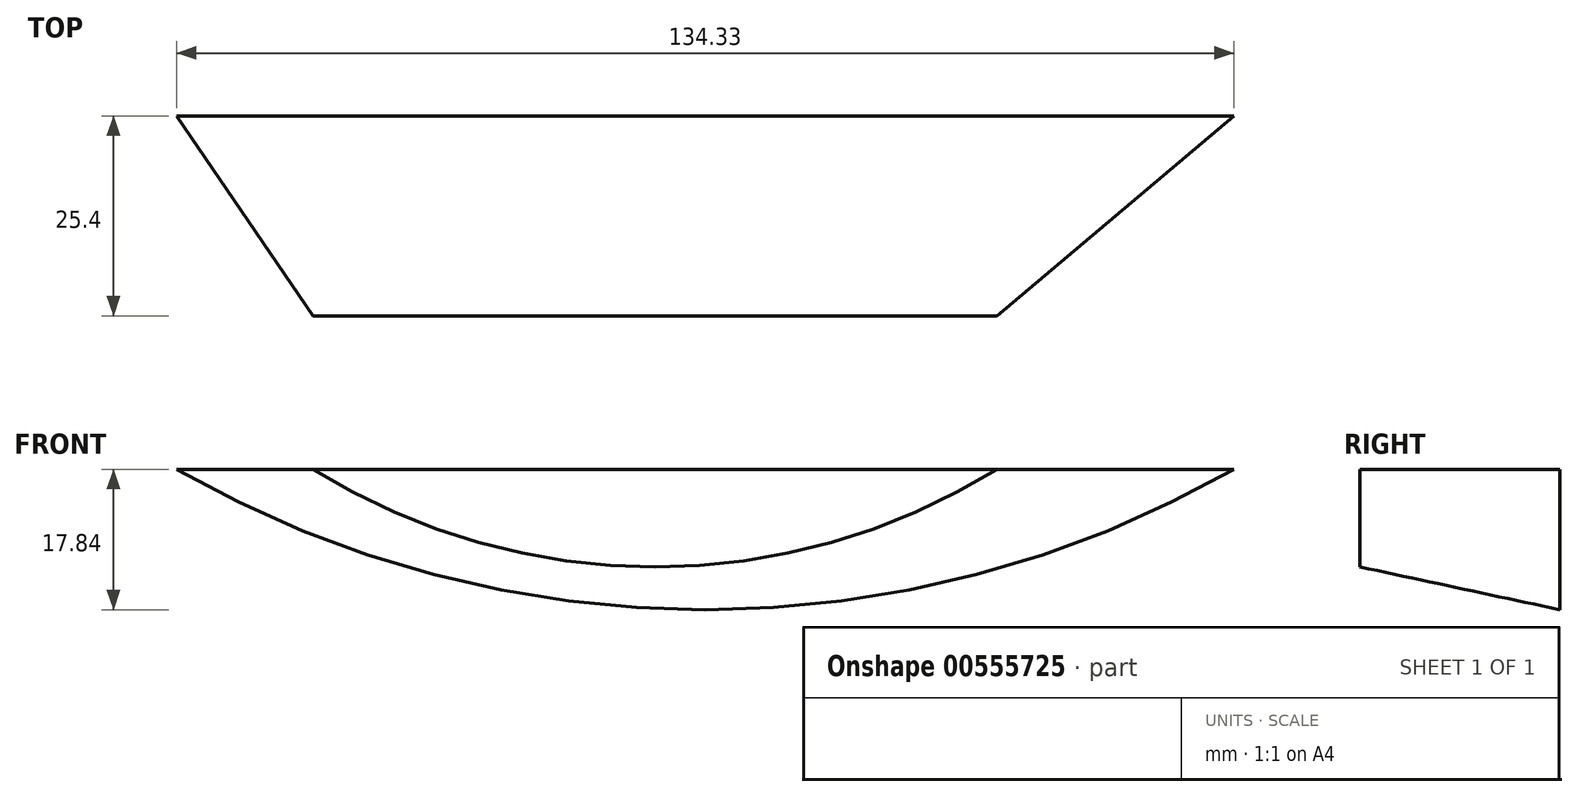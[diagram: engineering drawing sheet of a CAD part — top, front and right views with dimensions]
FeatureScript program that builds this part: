
annotation { "Feature Type Name" : "Feature", "Feature Type Description" : "" }
export const myFeature = defineFeature(function(context is Context, id is Id, definition is map)
    precondition{}
    {
        {
            var Q0;
            Q0=qCreatedBy(makeId("Top.planeOp"),FACE);
            var sketch = newSketch(context, id + "F0", { "sketchPlane" : qUnion([Q0])});
            skLineSegment(sketch, "E0", {"start": v(-69.36, 0) * mm, "end": v(64.97, 0) * mm});
            skLineSegment(sketch, "E1", {"start": v(64.97, 0) * mm, "end": v(64.97, -7.73) * mm});
            skLineSegment(sketch, "E2", {"start": v(-69.36, 0) * mm, "end": v(-69.36, -7.73) * mm});
            skArc(sketch, "E3", {"start": v(-69.36, -7.73) * mm, "mid": v(-2.2, -21.41) * mm, "end": v(64.97, -7.73) * mm});
            skLineSegment(sketch, "E4", {"start": v(64.97, -7.73) * mm, "end": v(-69.36, -7.73) * mm});
            skSolve(sketch);
        }
        {
            var Q0;
            Q0=qCreatedBy(makeId("Front.planeOp"),FACE);
            var sketch = newSketch(context, id + "F1", { "sketchPlane" : qUnion([Q0])});
            skLineSegment(sketch, "E5.0", {"start": v(-69.36, 0) * mm, "end": v(64.97, 0) * mm});
            skArc(sketch, "E6", {"start": v(-69.36, 0) * mm, "mid": v(-2.2, -17.84) * mm, "end": v(64.97, 0) * mm});
            skSolve(sketch);
        }
        {
            var Q0;
            Q0=qCreatedBy(makeId("Front.planeOp"),FACE);
            cPlane(context, id + "F2", {"entities" : qUnion([Q0]), "cplaneType" : CPlaneType.OFFSET, "offset" : 25.4 * mm, "width" : 152.4 * mm, "height" : 152.4 * mm});
        }
        {
            var Q0;
            Q0=qCreatedBy(id+"F2.planeOp",FACE);
            var sketch = newSketch(context, id + "F3", { "sketchPlane" : qUnion([Q0])});
            skLineSegment(sketch, "E7", {"start": v(34.89, 0) * mm, "end": v(-52.02, 0) * mm});
            skArc(sketch, "E8", {"start": v(-52.02, 0) * mm, "mid": v(-8.57, -12.4) * mm, "end": v(34.89, 0) * mm});
            skSolve(sketch);
        }
        {
            var Q0;
            Q0=makeQuery(id+"F1.imprint","IMPRINT",FACE,{"disambiguationData":[TD([[makeQuery(id+"F1.imprint","IMPRINT",EDGE,{"derivedFrom":sQuery(id+"F1.wireOp",EDGE,"E5.0")}),-1.0]])]});
            var Q1;
            Q1=makeQuery(id+"F3.imprint","IMPRINT",FACE,{"disambiguationData":[TD([[makeQuery(id+"F3.imprint","IMPRINT",EDGE,{"derivedFrom":sQuery(id+"F3.wireOp",EDGE,"E7")}),1.0]])]});
            var Q2;
            Q2=makeQuery(id+"F1.imprint","IMPRINT",FACE,{"disambiguationData":[TD([[makeQuery(id+"F1.imprint","IMPRINT",EDGE,{"derivedFrom":sQuery(id+"F1.wireOp",EDGE,"E5.0")}),-1.0]])]});
            var Q3;
            Q3=makeQuery(id+"F3.imprint","IMPRINT",FACE,{"disambiguationData":[TD([[makeQuery(id+"F3.imprint","IMPRINT",EDGE,{"derivedFrom":sQuery(id+"F3.wireOp",EDGE,"E7")}),1.0]])]});
            loft(context, id + "F4", {"bodyType" : ToolBodyType.SURFACE, "sheetProfilesArray" : [{ "sheetProfileEntities" : qUnion([Q0]) }, { "sheetProfileEntities" : qUnion([Q1]) }], "wireProfilesArray" : [{ "wireProfileEntities" : qUnion([Q2]) }, { "wireProfileEntities" : qUnion([Q3]) }]});
        }
    });
